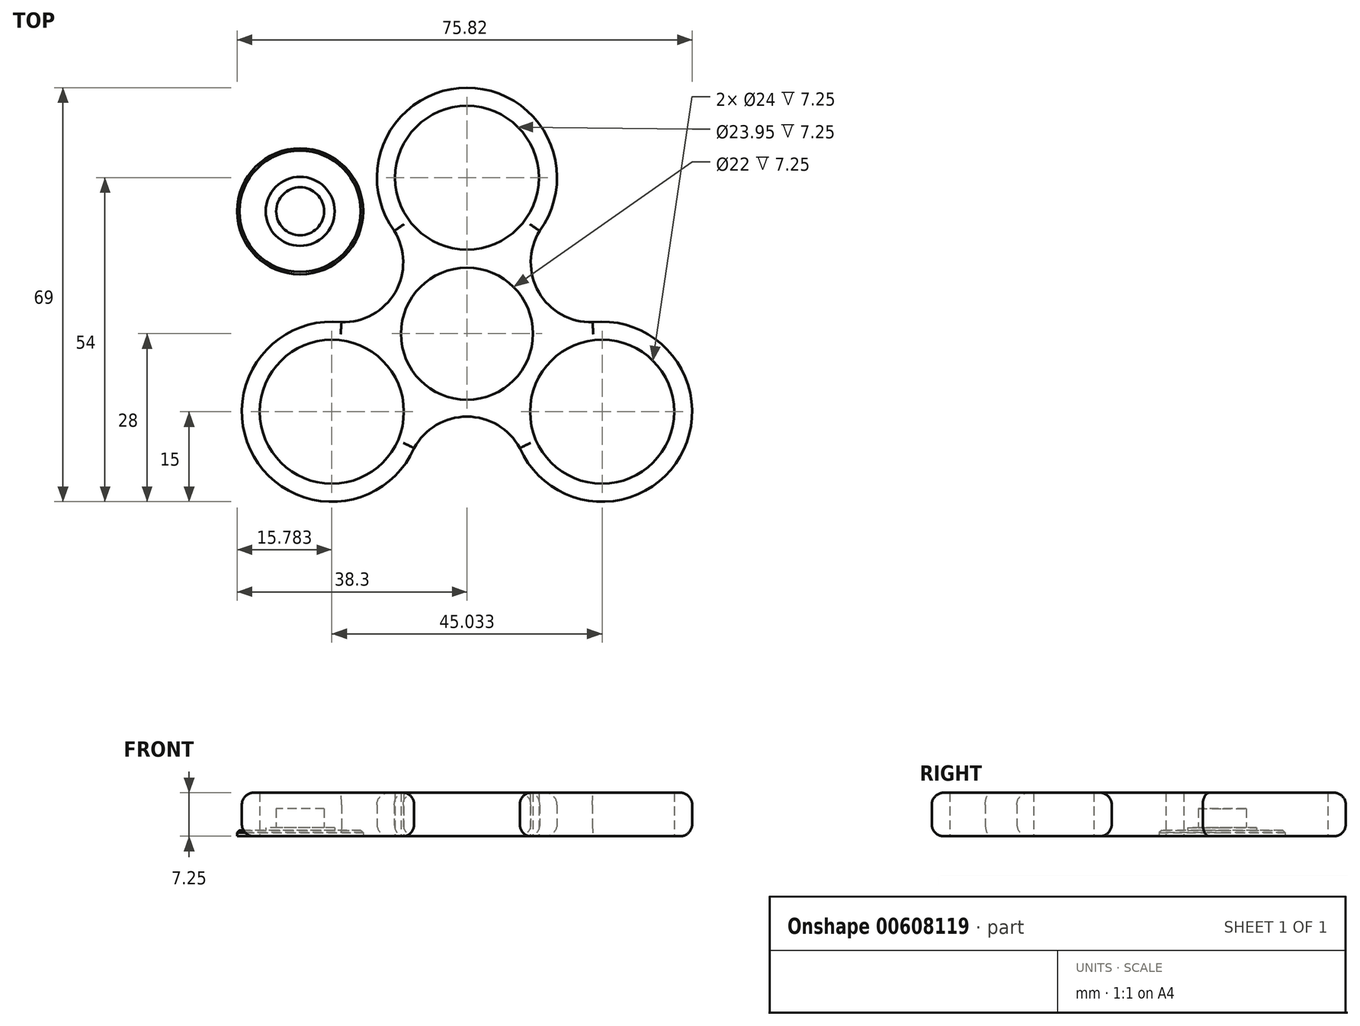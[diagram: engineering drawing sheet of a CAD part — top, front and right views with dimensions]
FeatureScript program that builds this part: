
annotation { "Feature Type Name" : "Feature", "Feature Type Description" : "" }
export const myFeature = defineFeature(function(context is Context, id is Id, definition is map)
    precondition{}
    {
        {
            var Q0;
            Q0=qCreatedBy(makeId("Top.planeOp"),FACE);
            var sketch = newSketch(context, id + "F0", { "sketchPlane" : qUnion([Q0])});
            skCircle(sketch, "E0", {"center": v(0, 26) * mm, "radius": 11.97 * mm});
            skArc(sketch, "E1", {"start": v(12.11, 17.15) * mm, "mid": v(0, 41) * mm, "end": v(-12.11, 17.15) * mm});
            skArc(sketch, "E2.1.0", {"start": v(-20.91, 1.91) * mm, "mid": v(-35.5, -20.5) * mm, "end": v(-8.8, -19.07) * mm});
            skCircle(sketch, "E2.1.1", {"center": v(-22.52, -13) * mm, "radius": 12 * mm});
            skCircle(sketch, "E2.1.2", {"center": v(-22.52, -13) * mm, "radius": 11.97 * mm});
            skArc(sketch, "E2.2.0", {"start": v(8.8, -19.07) * mm, "mid": v(35.5, -20.5) * mm, "end": v(20.91, 1.91) * mm});
            skCircle(sketch, "E2.2.1", {"center": v(22.52, -13) * mm, "radius": 12 * mm});
            skCircle(sketch, "E2.2.2", {"center": v(22.52, -13) * mm, "radius": 11.97 * mm});
            skPoint(sketch, "E2.center", {"position": v(0, 0) * mm});
            skCircle(sketch, "E3", {"center": v(0, 0) * mm, "radius": 11 * mm});
            skCircle(sketch, "E4", {"center": v(0, 0) * mm, "radius": 21 * mm, "construction": true});
            skArc(sketch, "E5", {"start": v(12.11, 17.15) * mm, "mid": v(11.97, 6.9) * mm, "end": v(20.91, 1.91) * mm});
            skArc(sketch, "E6.1.0", {"start": v(-20.91, 1.91) * mm, "mid": v(-11.97, 6.9) * mm, "end": v(-12.11, 17.15) * mm});
            skArc(sketch, "E6.2.0", {"start": v(8.8, -19.07) * mm, "mid": v(0, -13.82) * mm, "end": v(-8.8, -19.07) * mm});
            skSolve(sketch);
        }
        {
            var Q0;
            Q0=makeQuery(id+"F0.imprint","IMPRINT",FACE,{"disambiguationData":[TD([[makeQuery(id+"F0.imprint","IMPRINT",EDGE,{"derivedFrom":sQuery(id+"F0.wireOp",EDGE,"E0")}),-1.0]])]});
            extrude(context, id + "F1", {"entities" : qUnion([Q0]), "depth" : 7.25 * mm, "offsetDistance" : 25 * mm});
        }
        {
            var Q0;
            Q0=makeQuery(id+"F1.opExtrude","CAP_EDGE",EDGE,{"disambiguationData":[OSD([sQuery(id+"F0.wireOp",EDGE,"E2.1.0")])],"isStart":false});
            var Q1;
            Q1=makeQuery(id+"F1.opExtrude","CAP_EDGE",EDGE,{"disambiguationData":[OSD([sQuery(id+"F0.wireOp",EDGE,"E1")])],"isStart":false});
            var Q2;
            Q2=makeQuery(id+"F1.opExtrude","CAP_EDGE",EDGE,{"disambiguationData":[OSD([sQuery(id+"F0.wireOp",EDGE,"E2.2.0")])],"isStart":false});
            var Q3;
            Q3=makeQuery(id+"F1.opExtrude","CAP_EDGE",EDGE,{"disambiguationData":[OSD([sQuery(id+"F0.wireOp",EDGE,"E2.1.0")])],"isStart":true});
            var Q4;
            Q4=makeQuery(id+"F1.opExtrude","CAP_EDGE",EDGE,{"disambiguationData":[OSD([sQuery(id+"F0.wireOp",EDGE,"E2.2.0")])],"isStart":true});
            var Q5;
            Q5=makeQuery(id+"F1.opExtrude","CAP_EDGE",EDGE,{"disambiguationData":[OSD([sQuery(id+"F0.wireOp",EDGE,"E1")])],"isStart":true});
            fillet(context, id + "F2", {"entities" : qUnion([Q0, Q1, Q2, Q3, Q4, Q5]), "radius" : 2 * mm, "tangentPropagation" : true, "allowEdgeOverflow" : false});
        }
        {
            var Q0;
            Q0=qCreatedBy(makeId("Top.planeOp"),FACE);
            var sketch = newSketch(context, id + "F3", { "sketchPlane" : qUnion([Q0])});
            skCircle(sketch, "E7", {"center": v(-27.8, 20.4) * mm, "radius": 10.5 * mm});
            skCircle(sketch, "E8", {"center": v(-27.8, 20.4) * mm, "radius": 5.75 * mm});
            skCircle(sketch, "E9", {"center": v(-27.8, 20.4) * mm, "radius": 4 * mm});
            skSolve(sketch);
        }
        {
            var Q0;
            Q0=makeQuery(id+"F3.imprint","IMPRINT",FACE,{"disambiguationData":[TD([[makeQuery(id+"F3.imprint","IMPRINT",EDGE,{"derivedFrom":sQuery(id+"F3.wireOp",EDGE,"E8")}),1.0]])]});
            extrude(context, id + "F4", {"entities" : qUnion([Q0]), "operationType" : NewBodyOperationType.ADD, "depth" : 1.4 * mm, "offsetDistance" : 25 * mm});
        }
        {
            var Q0;
            Q0=makeQuery(id+"F3.imprint","IMPRINT",FACE,{"disambiguationData":[TD([[makeQuery(id+"F3.imprint","IMPRINT",EDGE,{"derivedFrom":sQuery(id+"F3.wireOp",EDGE,"E7")}),1.0]])]});
            extrude(context, id + "F5", {"entities" : qUnion([Q0]), "operationType" : NewBodyOperationType.ADD, "depth" : 1 * mm, "offsetDistance" : 25 * mm});
        }
        {
            var Q0;
            Q0=makeQuery(id+"F3.imprint","IMPRINT",FACE,{"disambiguationData":[TD([[makeQuery(id+"F3.imprint","IMPRINT",EDGE,{"derivedFrom":sQuery(id+"F3.wireOp",EDGE,"E9")}),1.0]])]});
            extrude(context, id + "F6", {"entities" : qUnion([Q0]), "operationType" : NewBodyOperationType.ADD, "depth" : 4.6 * mm, "offsetDistance" : 25 * mm});
        }
        {
            var Q0;
            Q0=makeQuery(id+"F5.opExtrude","CAP_EDGE",EDGE,{"disambiguationData":[OSD([sQuery(id+"F3.wireOp",EDGE,"E7")])],"isStart":false});
            chamfer(context, id + "F7", {"entities" : qUnion([Q0]), "width" : .4 * mm, "tangentPropagation" : true});
        }
    });
